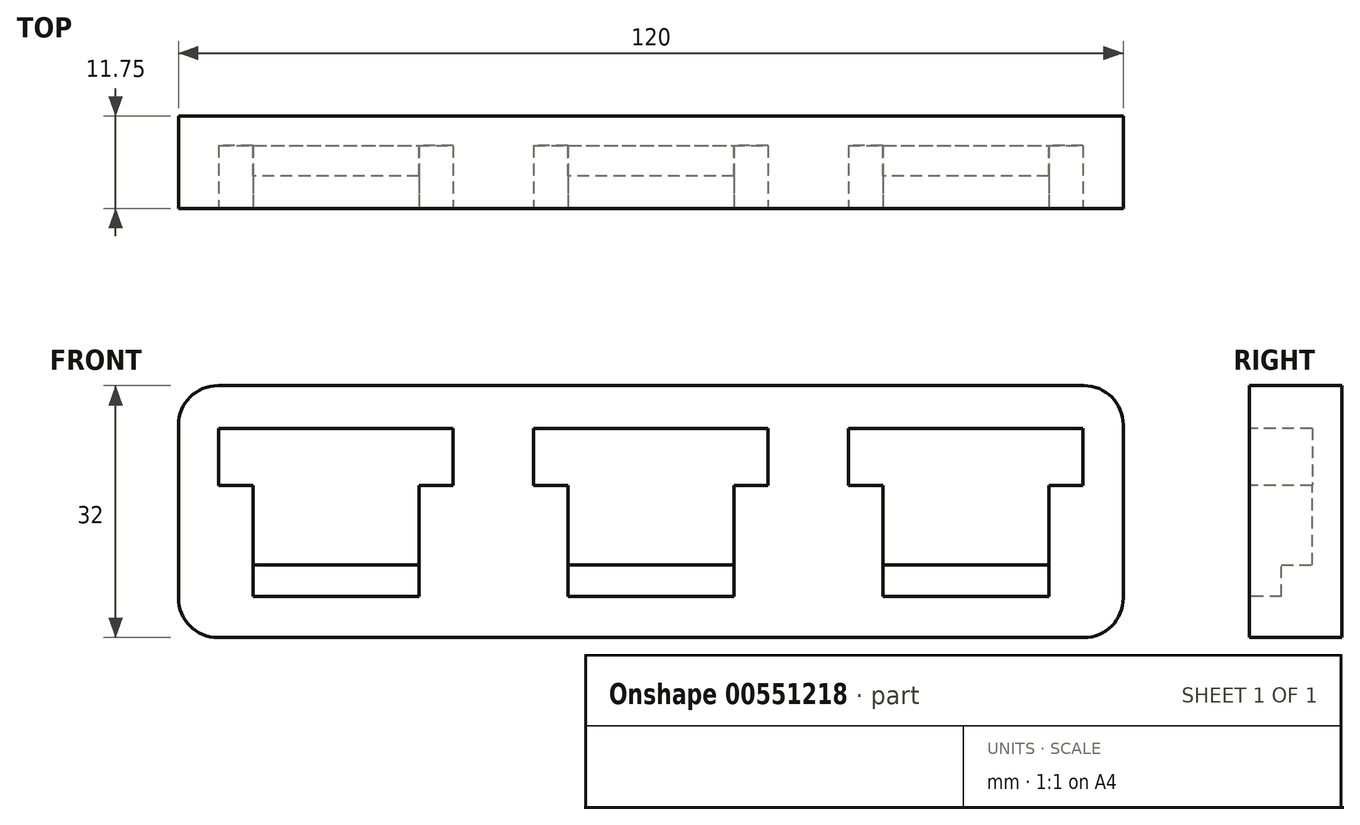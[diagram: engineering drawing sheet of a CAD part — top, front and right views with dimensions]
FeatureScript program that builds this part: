
annotation { "Feature Type Name" : "Feature", "Feature Type Description" : "" }
export const myFeature = defineFeature(function(context is Context, id is Id, definition is map)
    precondition{}
    {
        {
            var Q0;
            Q0=qCreatedBy(makeId("Front.planeOp"),FACE);
            var sketch = newSketch(context, id + "F0", { "sketchPlane" : qUnion([Q0])});
            skLineSegment(sketch, "E0.bottom", {"start": v(-120, 16) * mm, "end": v(120, 16) * mm});
            skLineSegment(sketch, "E0.top", {"start": v(-120, -16) * mm, "end": v(120, -16) * mm});
            skLineSegment(sketch, "E0.left", {"start": v(-120, 16) * mm, "end": v(-120, -16) * mm});
            skLineSegment(sketch, "E0.right", {"start": v(120, 16) * mm, "end": v(120, -16) * mm});
            skSolve(sketch);
        }
        {
            var Q0;
            Q0 = qSketchRegion(id + "F0", true);
            extrude(context, id + "F1", {"entities" : qUnion([Q0]), "depth" : 11.75 * mm, "offsetDistance" : 25 * mm});
        }
        {
            var Q0;
            Q0=makeQuery(id+"F1.opExtrude","CAP_FACE",FACE,{"disambiguationData":[OSD([sQuery(id+"F0.wireOp",EDGE,"E0.bottom"),sQuery(id+"F0.wireOp",EDGE,"E0.top"),sQuery(id+"F0.wireOp",EDGE,"E0.left"),sQuery(id+"F0.wireOp",EDGE,"E0.right")])],"isStart":true});
            var sketch = newSketch(context, id + "F2", { "sketchPlane" : qUnion([Q0])});
            skCircle(sketch, "E1", {"center": v(-105, -8) * mm, "radius": 6.38 * mm});
            skCircle(sketch, "E2.0.1.0", {"center": v(-105, 8) * mm, "radius": 6.38 * mm});
            skCircle(sketch, "E2.1.0.0", {"center": v(-55, -8) * mm, "radius": 6.38 * mm});
            skCircle(sketch, "E2.1.1.0", {"center": v(-55, 8) * mm, "radius": 6.38 * mm});
            skCircle(sketch, "E2.2.0.0", {"center": v(-5, -8) * mm, "radius": 6.38 * mm});
            skCircle(sketch, "E2.2.1.0", {"center": v(-5, 8) * mm, "radius": 6.38 * mm});
            skCircle(sketch, "E2.3.0.0", {"center": v(45, -8) * mm, "radius": 6.38 * mm});
            skCircle(sketch, "E2.3.1.0", {"center": v(45, 8) * mm, "radius": 6.38 * mm});
            skCircle(sketch, "E2.4.0.0", {"center": v(95, -8) * mm, "radius": 6.38 * mm});
            skCircle(sketch, "E2.4.1.0", {"center": v(95, 8) * mm, "radius": 6.38 * mm});
            skLineSegment(sketch, "E2.direction1", {"start": v(-127.25, -8) * mm, "end": v(-77.25, -8) * mm, "construction": true});
            skLineSegment(sketch, "E2.direction2", {"start": v(-127.25, -8) * mm, "end": v(-127.25, 8) * mm, "construction": true});
            skSolve(sketch);
        }
        {
            var Q0;
            Q0=makeQuery(id+"F1.opExtrude","CAP_FACE",FACE,{"disambiguationData":[OSD([sQuery(id+"F0.wireOp",EDGE,"E0.bottom"),sQuery(id+"F0.wireOp",EDGE,"E0.top"),sQuery(id+"F0.wireOp",EDGE,"E0.left"),sQuery(id+"F0.wireOp",EDGE,"E0.right")])],"isStart":false});
            var sketch = newSketch(context, id + "F3", { "sketchPlane" : qUnion([Q0])});
            skLineSegment(sketch, "E3", {"start": v(85.1, 10.58) * mm, "end": v(114.9, 10.58) * mm});
            skLineSegment(sketch, "E4", {"start": v(114.9, 10.58) * mm, "end": v(114.9, 3.32) * mm});
            skLineSegment(sketch, "E5", {"start": v(114.9, 3.32) * mm, "end": v(110.55, 3.32) * mm});
            skLineSegment(sketch, "E6", {"start": v(110.55, 3.32) * mm, "end": v(110.55, -10.75) * mm});
            skLineSegment(sketch, "E7", {"start": v(110.55, -10.75) * mm, "end": v(89.45, -10.75) * mm});
            skLineSegment(sketch, "E8", {"start": v(89.45, -10.75) * mm, "end": v(89.45, 3.32) * mm});
            skLineSegment(sketch, "E9", {"start": v(89.45, 3.32) * mm, "end": v(85.1, 3.32) * mm});
            skLineSegment(sketch, "E10", {"start": v(85.1, 3.32) * mm, "end": v(85.1, 10.58) * mm});
            skLineSegment(sketch, "E11.1.0.0", {"start": v(45.1, 10.58) * mm, "end": v(74.9, 10.58) * mm});
            skLineSegment(sketch, "E11.1.0.1", {"start": v(74.9, 10.58) * mm, "end": v(74.9, 3.32) * mm});
            skLineSegment(sketch, "E11.1.0.2", {"start": v(74.9, 3.32) * mm, "end": v(70.55, 3.32) * mm});
            skLineSegment(sketch, "E11.1.0.3", {"start": v(70.55, 3.32) * mm, "end": v(70.55, -10.75) * mm});
            skLineSegment(sketch, "E11.1.0.4", {"start": v(70.55, -10.75) * mm, "end": v(49.45, -10.75) * mm});
            skLineSegment(sketch, "E11.1.0.5", {"start": v(49.45, -10.75) * mm, "end": v(49.45, 3.32) * mm});
            skLineSegment(sketch, "E11.1.0.6", {"start": v(49.45, 3.32) * mm, "end": v(45.1, 3.32) * mm});
            skLineSegment(sketch, "E11.1.0.7", {"start": v(45.1, 3.32) * mm, "end": v(45.1, 10.58) * mm});
            skLineSegment(sketch, "E11.2.0.0", {"start": v(5.1, 10.58) * mm, "end": v(34.9, 10.58) * mm});
            skLineSegment(sketch, "E11.2.0.1", {"start": v(34.9, 10.58) * mm, "end": v(34.9, 3.32) * mm});
            skLineSegment(sketch, "E11.2.0.2", {"start": v(34.9, 3.32) * mm, "end": v(30.55, 3.32) * mm});
            skLineSegment(sketch, "E11.2.0.3", {"start": v(30.55, 3.32) * mm, "end": v(30.55, -10.75) * mm});
            skLineSegment(sketch, "E11.2.0.4", {"start": v(30.55, -10.75) * mm, "end": v(9.45, -10.75) * mm});
            skLineSegment(sketch, "E11.2.0.5", {"start": v(9.45, -10.75) * mm, "end": v(9.45, 3.32) * mm});
            skLineSegment(sketch, "E11.2.0.6", {"start": v(9.45, 3.32) * mm, "end": v(5.1, 3.32) * mm});
            skLineSegment(sketch, "E11.2.0.7", {"start": v(5.1, 3.32) * mm, "end": v(5.1, 10.58) * mm});
            skLineSegment(sketch, "E11.direction1", {"start": v(85.1, 10.58) * mm, "end": v(45.1, 10.58) * mm, "construction": true});
            skLineSegment(sketch, "E12.0.3.0", {"start": v(-34.9, 10.58) * mm, "end": v(-5.1, 10.58) * mm});
            skLineSegment(sketch, "E12.3.3.0", {"start": v(-5.1, 10.58) * mm, "end": v(-5.1, 3.32) * mm});
            skLineSegment(sketch, "E12.6.3.0", {"start": v(-5.1, 3.32) * mm, "end": v(-9.45, 3.32) * mm});
            skLineSegment(sketch, "E12.9.3.0", {"start": v(-9.45, 3.32) * mm, "end": v(-9.45, -10.75) * mm});
            skLineSegment(sketch, "E12.12.3.0", {"start": v(-9.45, -10.75) * mm, "end": v(-30.55, -10.75) * mm});
            skLineSegment(sketch, "E12.15.3.0", {"start": v(-30.55, -10.75) * mm, "end": v(-30.55, 3.32) * mm});
            skLineSegment(sketch, "E12.18.3.0", {"start": v(-30.55, 3.32) * mm, "end": v(-34.9, 3.32) * mm});
            skLineSegment(sketch, "E12.21.3.0", {"start": v(-34.9, 3.32) * mm, "end": v(-34.9, 10.58) * mm});
            skLineSegment(sketch, "E12.0.4.0", {"start": v(-74.9, 10.58) * mm, "end": v(-45.1, 10.58) * mm});
            skLineSegment(sketch, "E12.3.4.0", {"start": v(-45.1, 10.58) * mm, "end": v(-45.1, 3.32) * mm});
            skLineSegment(sketch, "E12.6.4.0", {"start": v(-45.1, 3.32) * mm, "end": v(-49.45, 3.32) * mm});
            skLineSegment(sketch, "E12.9.4.0", {"start": v(-49.45, 3.32) * mm, "end": v(-49.45, -10.75) * mm});
            skLineSegment(sketch, "E12.12.4.0", {"start": v(-49.45, -10.75) * mm, "end": v(-70.55, -10.75) * mm});
            skLineSegment(sketch, "E12.15.4.0", {"start": v(-70.55, -10.75) * mm, "end": v(-70.55, 3.32) * mm});
            skLineSegment(sketch, "E12.18.4.0", {"start": v(-70.55, 3.32) * mm, "end": v(-74.9, 3.32) * mm});
            skLineSegment(sketch, "E12.21.4.0", {"start": v(-74.9, 3.32) * mm, "end": v(-74.9, 10.58) * mm});
            skLineSegment(sketch, "E12.0.5.0", {"start": v(-114.9, 10.58) * mm, "end": v(-85.1, 10.58) * mm});
            skLineSegment(sketch, "E12.3.5.0", {"start": v(-85.1, 10.58) * mm, "end": v(-85.1, 3.32) * mm});
            skLineSegment(sketch, "E12.6.5.0", {"start": v(-85.1, 3.32) * mm, "end": v(-89.45, 3.32) * mm});
            skLineSegment(sketch, "E12.9.5.0", {"start": v(-89.45, 3.32) * mm, "end": v(-89.45, -10.75) * mm});
            skLineSegment(sketch, "E12.12.5.0", {"start": v(-89.45, -10.75) * mm, "end": v(-110.55, -10.75) * mm});
            skLineSegment(sketch, "E12.15.5.0", {"start": v(-110.55, -10.75) * mm, "end": v(-110.55, 3.32) * mm});
            skLineSegment(sketch, "E12.18.5.0", {"start": v(-110.55, 3.32) * mm, "end": v(-114.9, 3.32) * mm});
            skLineSegment(sketch, "E12.21.5.0", {"start": v(-114.9, 3.32) * mm, "end": v(-114.9, 10.58) * mm});
            skSolve(sketch);
        }
        {
            var Q0;
            Q0 = qSketchRegion(id + "F3", true);
            extrude(context, id + "F4", {"entities" : qUnion([Q0]), "operationType" : NewBodyOperationType.REMOVE, "oppositeDirection" : true, "depth" : 8 * mm, "offsetDistance" : 25 * mm});
        }
        {
            var Q0;
            Q0=makeQuery(id+"F4.boolean.opBoolean","COPY",FACE,{"derivedFrom":makeQuery(id+"F4.opExtrude","CAP_FACE",FACE,{"disambiguationData":[OSD([sQuery(id+"F3.wireOp",EDGE,"E3"),sQuery(id+"F3.wireOp",EDGE,"E4"),sQuery(id+"F3.wireOp",EDGE,"E5"),sQuery(id+"F3.wireOp",EDGE,"E6"),sQuery(id+"F3.wireOp",EDGE,"E7"),sQuery(id+"F3.wireOp",EDGE,"E8"),sQuery(id+"F3.wireOp",EDGE,"E9"),sQuery(id+"F3.wireOp",EDGE,"E10")])],"isStart":false})});
            var sketch = newSketch(context, id + "F5", { "sketchPlane" : qUnion([Q0])});
            skLineSegment(sketch, "E13", {"start": v(89.45, -6.75) * mm, "end": v(110.55, -6.75) * mm});
            skLineSegment(sketch, "E14", {"start": v(110.55, -6.75) * mm, "end": v(110.55, -10.75) * mm});
            skLineSegment(sketch, "E15", {"start": v(110.55, -10.75) * mm, "end": v(89.45, -10.75) * mm});
            skLineSegment(sketch, "E16", {"start": v(89.45, -10.75) * mm, "end": v(89.45, -6.75) * mm});
            skLineSegment(sketch, "E17.1.0.0", {"start": v(49.45, -6.75) * mm, "end": v(70.55, -6.75) * mm});
            skLineSegment(sketch, "E17.1.0.1", {"start": v(70.55, -6.75) * mm, "end": v(70.55, -10.75) * mm});
            skLineSegment(sketch, "E17.1.0.2", {"start": v(70.55, -10.75) * mm, "end": v(49.45, -10.75) * mm});
            skLineSegment(sketch, "E17.1.0.3", {"start": v(49.45, -10.75) * mm, "end": v(49.45, -6.75) * mm});
            skLineSegment(sketch, "E17.2.0.0", {"start": v(9.45, -6.75) * mm, "end": v(30.55, -6.75) * mm});
            skLineSegment(sketch, "E17.2.0.1", {"start": v(30.55, -6.75) * mm, "end": v(30.55, -10.75) * mm});
            skLineSegment(sketch, "E17.2.0.2", {"start": v(30.55, -10.75) * mm, "end": v(9.45, -10.75) * mm});
            skLineSegment(sketch, "E17.2.0.3", {"start": v(9.45, -10.75) * mm, "end": v(9.45, -6.75) * mm});
            skLineSegment(sketch, "E17.3.0.0", {"start": v(-30.55, -6.75) * mm, "end": v(-9.45, -6.75) * mm});
            skLineSegment(sketch, "E17.3.0.1", {"start": v(-9.45, -6.75) * mm, "end": v(-9.45, -10.75) * mm});
            skLineSegment(sketch, "E17.3.0.2", {"start": v(-9.45, -10.75) * mm, "end": v(-30.55, -10.75) * mm});
            skLineSegment(sketch, "E17.3.0.3", {"start": v(-30.55, -10.75) * mm, "end": v(-30.55, -6.75) * mm});
            skLineSegment(sketch, "E17.4.0.0", {"start": v(-70.55, -6.75) * mm, "end": v(-49.45, -6.75) * mm});
            skLineSegment(sketch, "E17.4.0.1", {"start": v(-49.45, -6.75) * mm, "end": v(-49.45, -10.75) * mm});
            skLineSegment(sketch, "E17.4.0.2", {"start": v(-49.45, -10.75) * mm, "end": v(-70.55, -10.75) * mm});
            skLineSegment(sketch, "E17.4.0.3", {"start": v(-70.55, -10.75) * mm, "end": v(-70.55, -6.75) * mm});
            skLineSegment(sketch, "E17.5.0.0", {"start": v(-110.55, -6.75) * mm, "end": v(-89.45, -6.75) * mm});
            skLineSegment(sketch, "E17.5.0.1", {"start": v(-89.45, -6.75) * mm, "end": v(-89.45, -10.75) * mm});
            skLineSegment(sketch, "E17.5.0.2", {"start": v(-89.45, -10.75) * mm, "end": v(-110.55, -10.75) * mm});
            skLineSegment(sketch, "E17.5.0.3", {"start": v(-110.55, -10.75) * mm, "end": v(-110.55, -6.75) * mm});
            skLineSegment(sketch, "E17.direction1", {"start": v(89.45, -6.75) * mm, "end": v(49.45, -6.75) * mm, "construction": true});
            skSolve(sketch);
        }
        {
            var Q0;
            Q0 = qSketchRegion(id + "F5", true);
            extrude(context, id + "F6", {"entities" : qUnion([Q0]), "operationType" : NewBodyOperationType.ADD, "depth" : 3.9 * mm, "offsetDistance" : 25 * mm});
        }
        {
            var Q0;
            Q0=qCreatedBy(makeId("Front.planeOp"),FACE);
            var sketch = newSketch(context, id + "F7", { "sketchPlane" : qUnion([Q0])});
            skLineSegment(sketch, "E18.bottom", {"start": v(0, -39.9) * mm, "end": v(-130, -39.9) * mm});
            skLineSegment(sketch, "E18.top", {"start": v(0, 40.1) * mm, "end": v(-130, 40.1) * mm});
            skLineSegment(sketch, "E18.left", {"start": v(0, -39.9) * mm, "end": v(0, 40.1) * mm});
            skLineSegment(sketch, "E18.right", {"start": v(-130, -39.9) * mm, "end": v(-130, 40.1) * mm});
            skSolve(sketch);
        }
        {
            var Q0;
            Q0 = qSketchRegion(id + "F7", true);
            extrude(context, id + "F8", {"entities" : qUnion([Q0]), "operationType" : NewBodyOperationType.REMOVE, "depth" : 30 * mm, "offsetDistance" : 25 * mm});
        }
        {
            var Q0;
            Q0=makeQuery(id+"F1.opExtrude","SWEPT_EDGE",EDGE,{"disambiguationData":[OSD([sQuery(id+"F0.wireOp",EDGE,"E0.top"),sQuery(id+"F0.wireOp",EDGE,"E0.right")])]});
            var Q1;
            Q1=makeQuery(id+"F1.opExtrude","SWEPT_EDGE",EDGE,{"disambiguationData":[OSD([sQuery(id+"F0.wireOp",EDGE,"E0.bottom"),sQuery(id+"F0.wireOp",EDGE,"E0.right")])]});
            var Q2;
            Q2=makeQuery(id+"F8.boolean.opBoolean","INTERSECT",EDGE,{"derivedFrom":[makeQuery(id+"F1.opExtrude","SWEPT_FACE",FACE,{"disambiguationData":[OSD([sQuery(id+"F0.wireOp",EDGE,"E0.top")])]}),makeQuery(id+"F8.opExtrude","SWEPT_FACE",FACE,{"disambiguationData":[OSD([sQuery(id+"F7.wireOp",EDGE,"E18.left")])]})]});
            var Q3;
            Q3=makeQuery(id+"F8.boolean.opBoolean","INTERSECT",EDGE,{"derivedFrom":[makeQuery(id+"F1.opExtrude","SWEPT_FACE",FACE,{"disambiguationData":[OSD([sQuery(id+"F0.wireOp",EDGE,"E0.bottom")])]}),makeQuery(id+"F8.opExtrude","SWEPT_FACE",FACE,{"disambiguationData":[OSD([sQuery(id+"F7.wireOp",EDGE,"E18.left")])]})]});
            fillet(context, id + "F9", {"entities" : qUnion([Q0, Q1, Q2, Q3]), "radius" : 5 * mm, "tangentPropagation" : true, "allowEdgeOverflow" : false});
        }
    });
